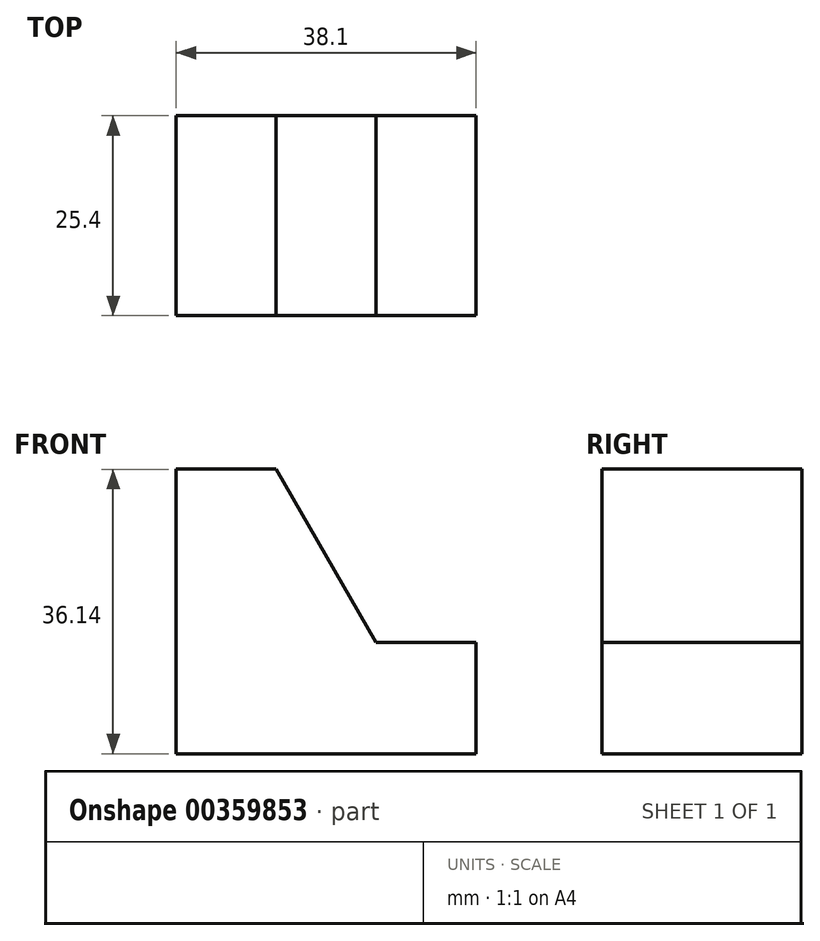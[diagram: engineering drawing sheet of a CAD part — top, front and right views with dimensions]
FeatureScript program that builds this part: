
annotation { "Feature Type Name" : "Feature", "Feature Type Description" : "" }
export const myFeature = defineFeature(function(context is Context, id is Id, definition is map)
    precondition{}
    {
        {
            var Q0;
            Q0=qCreatedBy(makeId("Front.planeOp"),FACE);
            var sketch = newSketch(context, id + "F0", { "sketchPlane" : qUnion([Q0])});
            skLineSegment(sketch, "E0", {"start": v(0, 0) * mm, "end": v(0, 36.14) * mm});
            skLineSegment(sketch, "E1", {"start": v(0, 36.14) * mm, "end": v(38.1, 36.14) * mm});
            skLineSegment(sketch, "E2", {"start": v(38.1, 36.14) * mm, "end": v(38.1, 0) * mm});
            skLineSegment(sketch, "E3", {"start": v(38.1, 0) * mm, "end": v(0, 0) * mm});
            skSolve(sketch);
        }
        {
            var Q0;
            Q0 = qSketchRegion(id + "F0", true);
            extrude(context, id + "F1", {"entities" : qUnion([Q0]), "depth" : 25.4 * mm});
        }
        {
            var Q0;
            Q0=makeQuery(id+"F1.opExtrude","CAP_FACE",FACE,{"disambiguationData":[OSD([sQuery(id+"F0.wireOp",EDGE,"E0"),sQuery(id+"F0.wireOp",EDGE,"E1"),sQuery(id+"F0.wireOp",EDGE,"E2"),sQuery(id+"F0.wireOp",EDGE,"E3")])],"isStart":false});
            var sketch = newSketch(context, id + "F2", { "sketchPlane" : qUnion([Q0])});
            skLineSegment(sketch, "E4", {"start": v(12.7, 36.14) * mm, "end": v(25.4, 14.14) * mm});
            skLineSegment(sketch, "E5", {"start": v(25.4, 14.14) * mm, "end": v(38.1, 14.14) * mm});
            skSolve(sketch);
        }
        {
            var Q0;
            Q0 = qSketchRegion(id + "F2", true);
            var Q1;
            {var subQ0=sQuery(id+"F2.wireOp",EDGE,"E4");Q1=makeQuery(id+"F2.imprint","IMPRINT",FACE,{"disambiguationData":[TD([[makeQuery(id+"F2.imprint","IMPRINT",EDGE,{"derivedFrom":subQ0}),1.0]])]});}
            extrude(context, id + "F3", {"entities" : qUnion([Q0, Q1]), "operationType" : NewBodyOperationType.REMOVE, "oppositeDirection" : true, "depth" : 25.4 * mm});
        }
    });
